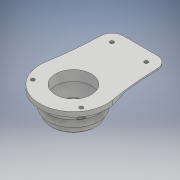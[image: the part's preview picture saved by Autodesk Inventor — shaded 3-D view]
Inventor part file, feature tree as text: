
AUTODESK INVENTOR PART (.ipt)
format: ipt  version: 2017 (Build 210142000, 142)  size: 636,416 bytes
history: native  units: mm
features: sketch x5, extrude x5, chamfer x4, fillet x2, plane x1, hole x1, reference x1
ambient origin geometry x8: Origin, YZ Plane, XZ Plane, XY Plane, X Axis, Y Axis, Z Axis, Center Point
bodies: Solid1 (feature_tree)
feature tree (19):
  sketch  "Sketch1"  dims[d0=42.0mm d1=17.5mm d2=0.0mm]
  plane  "Work Plane1"
  extrude  "Extrusion1"  Depth=17.5mm TaperAngle=0.0deg
  extrude  "Extrusion2"  Depth=13.0mm TaperAngle=0.0deg
  extrude  "Extrusion3"  Depth=8.0mm TaperAngle=0.0deg
  chamfer  "Chamfer1"  Distance=0.8mm Angle=45.0deg
  chamfer  "Chamfer2"  Distance=1.0mm Angle=45.0deg
  extrude  "Extrusion4"  Depth=3.25mm TaperAngle=45.0deg
  chamfer  "Chamfer3"  Distance=10.25mm Angle=45.0deg
  fillet  "Fillet1"  Radius=7.0mm
  chamfer  "Chamfer4"  Distance=7.2mm
  fillet  "Fillet2"  Radius=7.2mm
  sketch  "Sketch5"  dims[d20=13.0mm d21=10.25mm d22=2.0mm d23=45.0deg d24=7.0mm d25=7.2mm d26=7.2mm d27=18.0mm d28=0.0mm d29=4.3mm d30=6.0mm d31=4.0mm d32=2.0mm d33=90.0deg d34=8.0mm d35=20.594885mm]
  extrude  "Extrusion5"  Depth=18.0mm TaperAngle=0.0deg
  hole  "Hole1"  [1 undecoded]
  reference  "Reference1"
  sketch  "Sketch2"  dims[d3=47.0mm d4=13.0mm d5=0.0mm]
  sketch  "Sketch3"  dims[d6=52.0mm d7=8.0mm d8=0.0mm d9=0.8mm d10=2.0mm d11=45.0deg d12=1.0mm d13=2.0mm d14=45.0deg]
  sketch  "Sketch4"  dims[d15=12.0mm d16=0.0mm d17=3.25mm d18=2.0mm d19=45.0deg]
note: 1 required parameter value undecoded (feature->parameter linkage not recoverable at this tier; creation-order binding heuristic only, values carry confidence <= 0.55)
